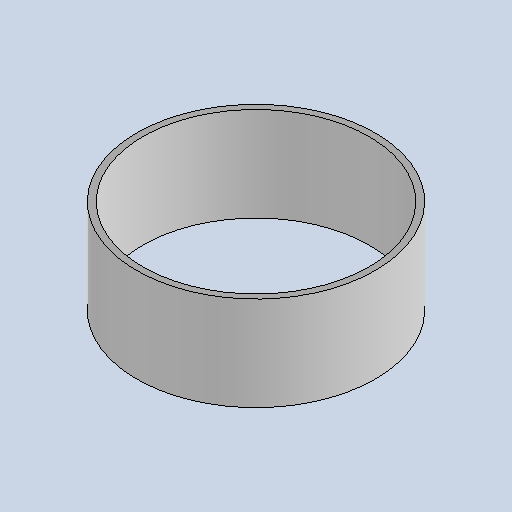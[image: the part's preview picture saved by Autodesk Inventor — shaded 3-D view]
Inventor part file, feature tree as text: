
AUTODESK INVENTOR PART (.ipt)
format: ipt  version: 2025.1 (Build 291241020, 241B)  size: 135,168 bytes
history: native  units: mm
features: extrude x1, sketch x1
ambient origin geometry x8: Origin, YZ Plane, XZ Plane, XY Plane, X Axis, Y Axis, Z Axis, Center Point
bodies: Solid1 (feature_tree)
feature tree (2):
  extrude  "Extrusion1"  Depth=30.0mm
  sketch  "Sketch1"  dims[d4=30.0mm d5=0.0mm d6=76.1mm d7=2.0mm]
